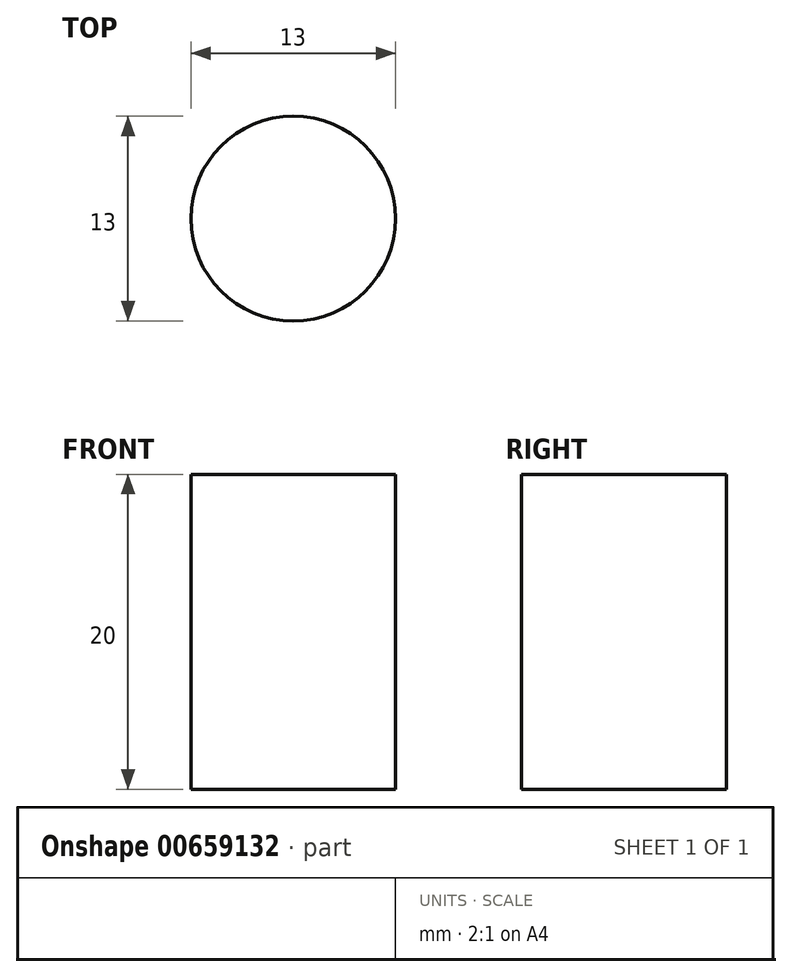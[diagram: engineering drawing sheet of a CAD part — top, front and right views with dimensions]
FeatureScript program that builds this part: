
annotation { "Feature Type Name" : "Feature", "Feature Type Description" : "" }
export const myFeature = defineFeature(function(context is Context, id is Id, definition is map)
    precondition{}
    {
        {
            var Q0;
            Q0=qCreatedBy(makeId("Top.planeOp"),FACE);
            var sketch = newSketch(context, id + "F0", { "sketchPlane" : qUnion([Q0])});
            skCircle(sketch, "E0", {"center": v(0, 0) * mm, "radius": 6.5 * mm});
            skSolve(sketch);
        }
        {
            var Q0;
            Q0 = qSketchRegion(id + "F0", true);
            extrude(context, id + "F1", {"entities" : qUnion([Q0]), "endBound" : BoundingType.SYMMETRIC, "depth" : 20 * mm, "offsetDistance" : 25 * mm});
        }
    });
